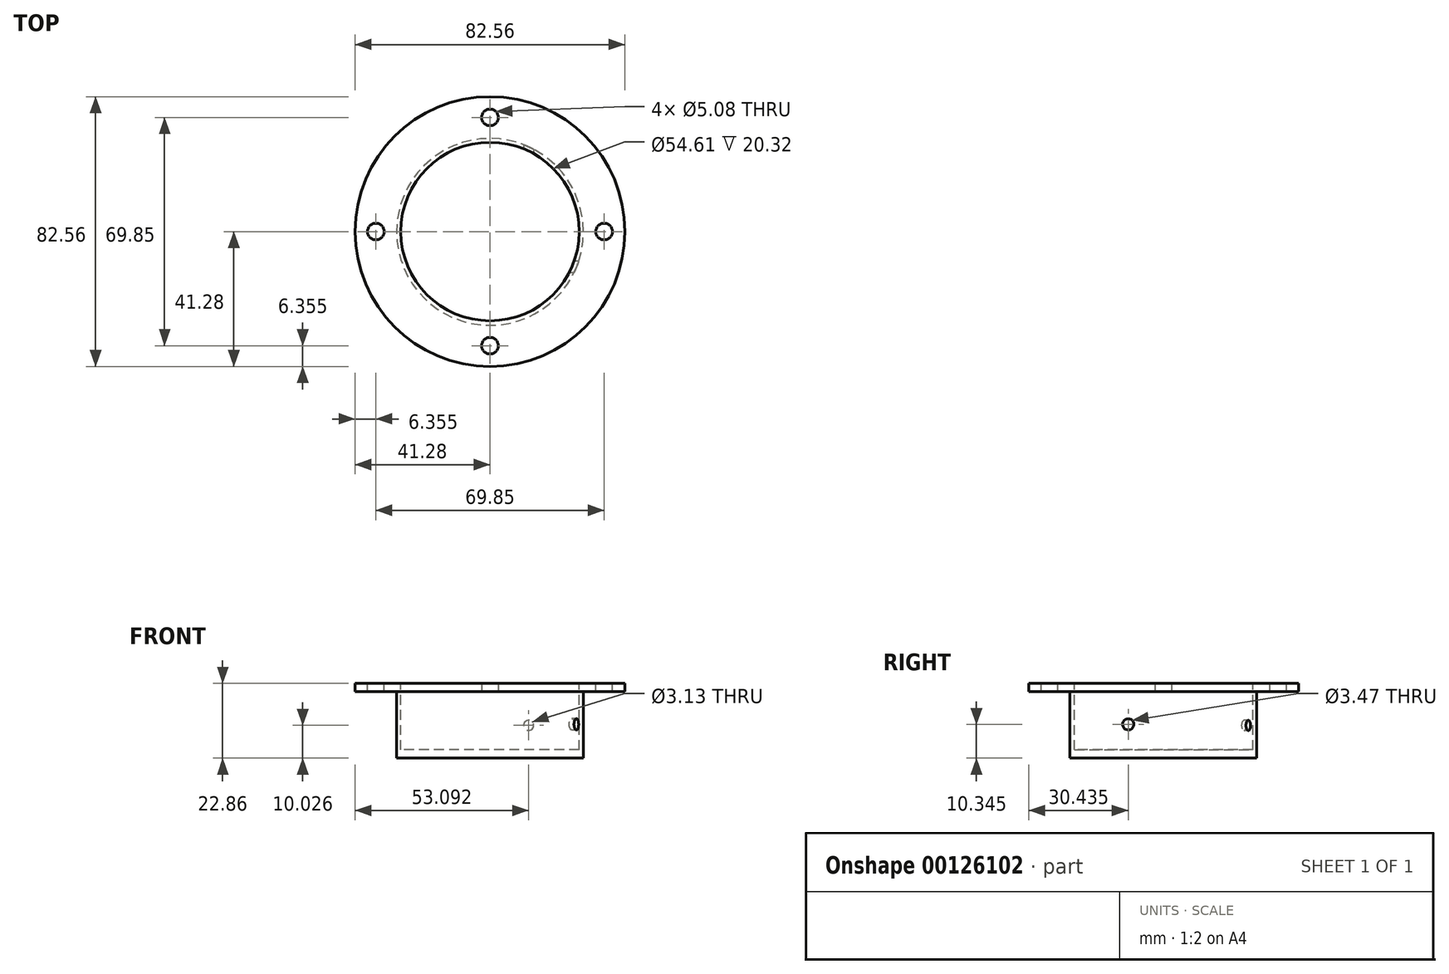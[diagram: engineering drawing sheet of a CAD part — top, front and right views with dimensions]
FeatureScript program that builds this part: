
annotation { "Feature Type Name" : "Feature", "Feature Type Description" : "" }
export const myFeature = defineFeature(function(context is Context, id is Id, definition is map)
    precondition{}
    {
        {
            var Q0;
            Q0=qCreatedBy(makeId("Top.planeOp"),FACE);
            var sketch = newSketch(context, id + "F0", { "sketchPlane" : qUnion([Q0])});
            skCircle(sketch, "E0", {"center": v(0, -0.1) * mm, "radius": 28.57 * mm});
            skSolve(sketch);
        }
        {
            var Q0;
            Q0 = qSketchRegion(id + "F0", true);
            extrude(context, id + "F1", {"entities" : qUnion([Q0]), "depth" : 20.32 * mm});
        }
        {
            var Q0;
            Q0=makeQuery(id+"F1.opExtrude","CAP_FACE",FACE,{"disambiguationData":[OSD([sQuery(id+"F0.wireOp",EDGE,"E0")])],"isStart":false});
            var sketch = newSketch(context, id + "F2", { "sketchPlane" : qUnion([Q0])});
            skCircle(sketch, "E1", {"center": v(0, 0) * mm, "radius": 27.3 * mm});
            skSolve(sketch);
        }
        {
            var Q0;
            Q0 = qSketchRegion(id + "F2", true);
            extrude(context, id + "F3", {"entities" : qUnion([Q0]), "operationType" : NewBodyOperationType.REMOVE, "oppositeDirection" : true, "depth" : 17.78 * mm});
        }
        {
            var Q0;
            Q0=qCreatedBy(makeId("Right.planeOp"),FACE);
            var sketch = newSketch(context, id + "F4", { "sketchPlane" : qUnion([Q0])});
            skCircle(sketch, "E2", {"center": v(-10.85, 10.35) * mm, "radius": 1.73 * mm});
            skPoint(sketch, "E2.first.point", {"position": v(-11.96, 11.67) * mm});
            skPoint(sketch, "E2.second.point", {"position": v(-9.11, 10.35) * mm});
            skPoint(sketch, "E2.third.point", {"position": v(-11.96, 9.02) * mm});
            skSolve(sketch);
        }
        {
            var Q0;
            Q0 = qSketchRegion(id + "F4", true);
            extrude(context, id + "F5", {"entities" : qUnion([Q0]), "operationType" : NewBodyOperationType.REMOVE, "endBound" : BoundingType.THROUGH_ALL, "depth" : 25.4 * mm});
        }
        {
            var Q0;
            Q0=qCreatedBy(makeId("Front.planeOp"),FACE);
            var sketch = newSketch(context, id + "F6", { "sketchPlane" : qUnion([Q0])});
            skCircle(sketch, "E3", {"center": v(11.81, 10.03) * mm, "radius": 1.56 * mm});
            skPoint(sketch, "E3.first.point", {"position": v(13.1, 10.91) * mm});
            skPoint(sketch, "E3.second.point", {"position": v(10.25, 9.97) * mm});
            skPoint(sketch, "E3.third.point", {"position": v(12.53, 8.64) * mm});
            skSolve(sketch);
        }
        {
            var Q0;
            Q0 = qSketchRegion(id + "F6", true);
            extrude(context, id + "F7", {"entities" : qUnion([Q0]), "operationType" : NewBodyOperationType.REMOVE, "endBound" : BoundingType.THROUGH_ALL, "oppositeDirection" : true, "depth" : 25.4 * mm});
        }
        {
            var Q0;
            Q0=makeQuery(id+"F1.opExtrude","CAP_FACE",FACE,{"disambiguationData":[OSD([sQuery(id+"F0.wireOp",EDGE,"E0")])],"isStart":false});
            var sketch = newSketch(context, id + "F8", { "sketchPlane" : qUnion([Q0])});
            skCircle(sketch, "E4", {"center": v(0, 0) * mm, "radius": 41.28 * mm});
            skSolve(sketch);
        }
        {
            var Q0;
            Q0 = qSketchRegion(id + "F8", true);
            extrude(context, id + "F9", {"entities" : qUnion([Q0]), "operationType" : NewBodyOperationType.ADD, "depth" : 2.54 * mm});
        }
        {
            var Q0;
            Q0=makeQuery(id+"F9.opExtrude","CAP_FACE",FACE,{"disambiguationData":[OSD([sQuery(id+"F8.wireOp",EDGE,"E4")])],"isStart":false});
            var sketch = newSketch(context, id + "F10", { "sketchPlane" : qUnion([Q0])});
            skCircle(sketch, "E5", {"center": v(0, 0) * mm, "radius": 27.3 * mm});
            skSolve(sketch);
        }
        {
            var Q0;
            Q0 = qSketchRegion(id + "F10", true);
            extrude(context, id + "F11", {"entities" : qUnion([Q0]), "operationType" : NewBodyOperationType.REMOVE, "oppositeDirection" : true, "depth" : 2.54 * mm});
        }
        {
            var Q0;
            Q0=qCreatedBy(makeId("Top.planeOp"),FACE);
            var sketch = newSketch(context, id + "F12", { "sketchPlane" : qUnion([Q0])});
            skCircle(sketch, "E6", {"center": v(0, 34.93) * mm, "radius": 2.54 * mm});
            skSolve(sketch);
        }
        {
            var Q0;
            Q0 = qSketchRegion(id + "F12", true);
            extrude(context, id + "F13", {"entities" : qUnion([Q0]), "operationType" : NewBodyOperationType.REMOVE, "endBound" : BoundingType.THROUGH_ALL, "depth" : 25.4 * mm});
        }
        {
            var Q0;
            Q0=makeQuery(id+"F9.opExtrude","CAP_FACE",FACE,{"disambiguationData":[OSD([sQuery(id+"F8.wireOp",EDGE,"E4")])],"isStart":false});
            var sketch = newSketch(context, id + "F14", { "sketchPlane" : qUnion([Q0])});
            skCircle(sketch, "E7", {"center": v(-34.93, 0) * mm, "radius": 2.54 * mm});
            skSolve(sketch);
        }
        {
            var Q0;
            Q0 = qSketchRegion(id + "F14", true);
            extrude(context, id + "F15", {"entities" : qUnion([Q0]), "operationType" : NewBodyOperationType.REMOVE, "endBound" : BoundingType.THROUGH_ALL, "oppositeDirection" : true, "depth" : 25.4 * mm});
        }
        {
            var Q0;
            Q0=makeQuery(id+"F9.opExtrude","CAP_FACE",FACE,{"disambiguationData":[OSD([sQuery(id+"F8.wireOp",EDGE,"E4")])],"isStart":false});
            var sketch = newSketch(context, id + "F16", { "sketchPlane" : qUnion([Q0])});
            skCircle(sketch, "E8", {"center": v(0, -34.93) * mm, "radius": 2.54 * mm});
            skSolve(sketch);
        }
        {
            var Q0;
            Q0 = qSketchRegion(id + "F16", true);
            extrude(context, id + "F17", {"entities" : qUnion([Q0]), "operationType" : NewBodyOperationType.REMOVE, "endBound" : BoundingType.THROUGH_ALL, "oppositeDirection" : true, "depth" : 25.4 * mm});
        }
        {
            var Q0;
            Q0=makeQuery(id+"F9.opExtrude","CAP_FACE",FACE,{"disambiguationData":[OSD([sQuery(id+"F8.wireOp",EDGE,"E4")])],"isStart":false});
            var sketch = newSketch(context, id + "F18", { "sketchPlane" : qUnion([Q0])});
            skCircle(sketch, "E9", {"center": v(34.93, 0) * mm, "radius": 2.54 * mm});
            skSolve(sketch);
        }
        {
            var Q0;
            Q0 = qSketchRegion(id + "F18", true);
            extrude(context, id + "F19", {"entities" : qUnion([Q0]), "operationType" : NewBodyOperationType.REMOVE, "endBound" : BoundingType.THROUGH_ALL, "oppositeDirection" : true, "depth" : 25.4 * mm});
        }
    });
